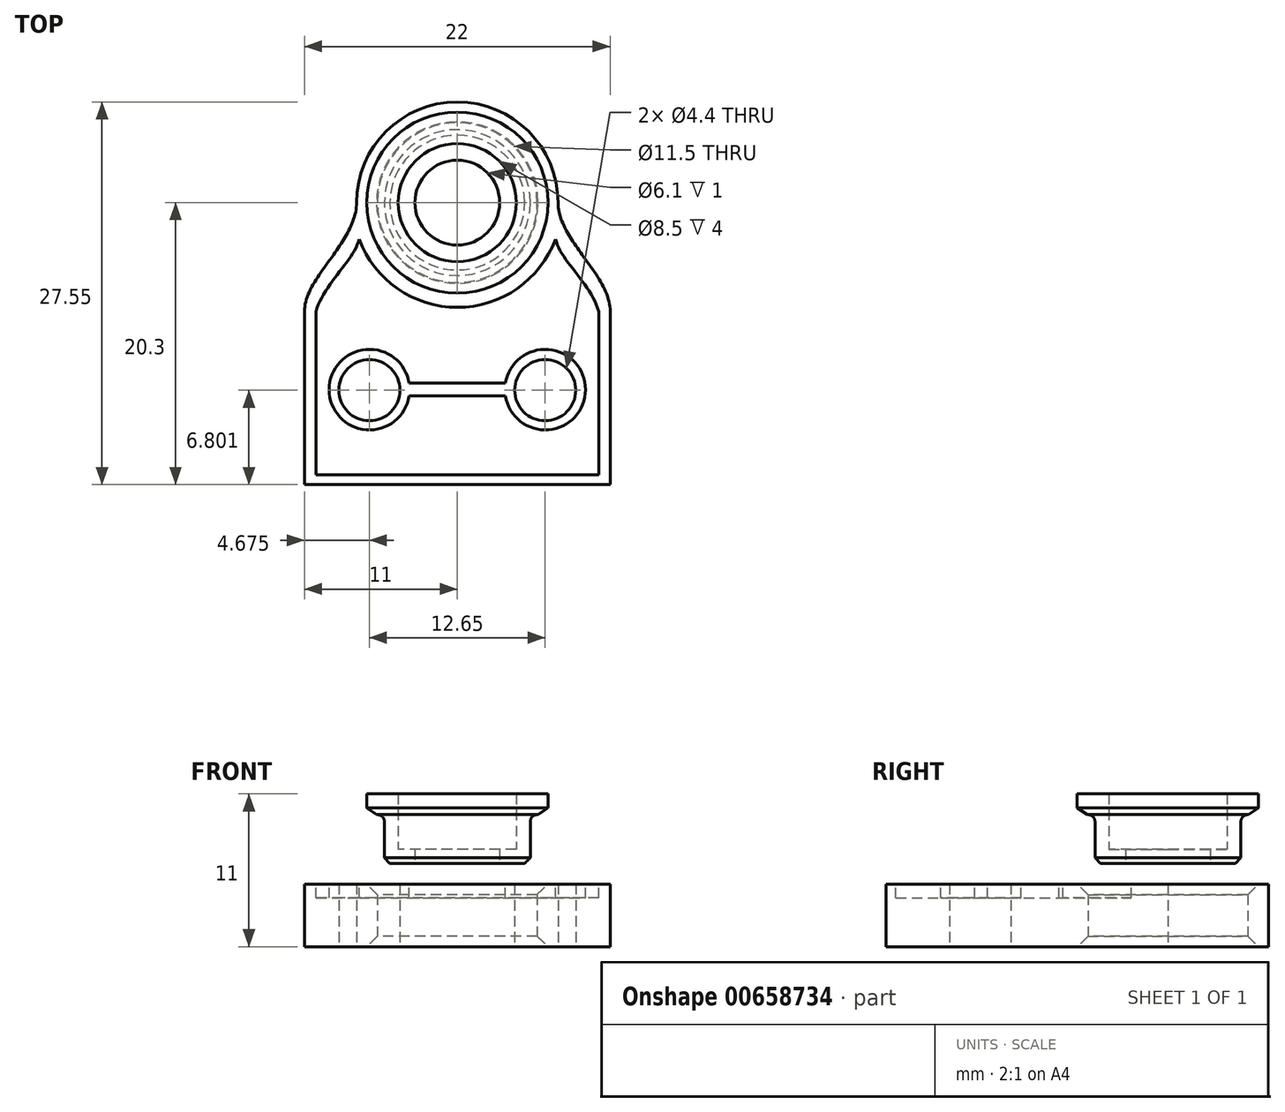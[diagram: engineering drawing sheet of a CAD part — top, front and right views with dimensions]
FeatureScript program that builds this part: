
annotation { "Feature Type Name" : "Feature", "Feature Type Description" : "" }
export const myFeature = defineFeature(function(context is Context, id is Id, definition is map)
    precondition{}
    {
        {
            var Q0;
            Q0=qCreatedBy(makeId("Top.planeOp"),FACE);
            var sketch = newSketch(context, id + "F0", { "sketchPlane" : qUnion([Q0])});
            skCircle(sketch, "E0", {"center": v(0, 0) * mm, "radius": 3.05 * mm});
            skCircle(sketch, "E1.0", {"center": v(0, 0) * mm, "radius": 4.25 * mm});
            skCircle(sketch, "E2.0", {"center": v(0, 0) * mm, "radius": 5.25 * mm});
            skSolve(sketch);
        }
        {
            var Q0;
            Q0=makeQuery(id+"F0.imprint","IMPRINT",FACE,{"disambiguationData":[TD([[makeQuery(id+"F0.imprint","IMPRINT",EDGE,{"derivedFrom":sQuery(id+"F0.wireOp",EDGE,"E0")}),-1.0]])]});
            extrude(context, id + "F1", {"entities" : qUnion([Q0]), "depth" : 1 * mm, "offsetDistance" : 25 * mm});
        }
        {
            var Q0;
            Q0=makeQuery(id+"F0.imprint","IMPRINT",FACE,{"disambiguationData":[TD([[makeQuery(id+"F0.imprint","IMPRINT",EDGE,{"derivedFrom":sQuery(id+"F0.wireOp",EDGE,"E1.0")}),-1.0]])]});
            extrude(context, id + "F2", {"entities" : qUnion([Q0]), "operationType" : NewBodyOperationType.ADD, "depth" : 5 * mm, "offsetDistance" : 25 * mm});
        }
        {
            var Q0;
            Q0=makeQuery(id+"F2.opExtrude","CAP_EDGE",EDGE,{"disambiguationData":[OSD([sQuery(id+"F0.wireOp",EDGE,"E2.0")])],"isStart":true});
            chamfer(context, id + "F3", {"entities" : qUnion([Q0]), "width" : .4 * mm, "tangentPropagation" : true});
        }
        {
            var Q0;
            Q0=qCreatedBy(makeId("Top.planeOp"),FACE);
            cPlane(context, id + "F4", {"entities" : qUnion([Q0]), "cplaneType" : CPlaneType.OFFSET, "offset" : 5 * mm, "width" : 150 * mm, "height" : 150 * mm});
        }
        {
            var Q0;
            Q0=qCreatedBy(id+"F4.planeOp",FACE);
            var sketch = newSketch(context, id + "F5", { "sketchPlane" : qUnion([Q0])});
            skCircle(sketch, "E3", {"center": v(0, 0) * mm, "radius": 4.84 * mm});
            skCircle(sketch, "E4", {"center": v(0, 0) * mm, "radius": 6.52 * mm});
            skSolve(sketch);
        }
        {
            var Q0;
            Q0 = qSketchRegion(id + "F5", true);
            extrude(context, id + "F6", {"entities" : qUnion([Q0]), "operationType" : NewBodyOperationType.ADD, "oppositeDirection" : true, "depth" : 1.5 * mm, "offsetDistance" : 25 * mm});
        }
        {
            var Q0;
            Q0=makeQuery(id+"F6.boolean.opBoolean","INTERSECT",EDGE,{"derivedFrom":[makeQuery(id+"F2.opExtrude","SWEPT_FACE",FACE,{"disambiguationData":[OSD([sQuery(id+"F0.wireOp",EDGE,"E2.0")])]}),makeQuery(id+"F6.opExtrude","CAP_FACE",FACE,{"disambiguationData":[OSD([sQuery(id+"F5.wireOp",EDGE,"E3"),sQuery(id+"F5.wireOp",EDGE,"E4")])],"isStart":false})]});
            fillet(context, id + "F7", {"entities" : qUnion([Q0]), "radius" : .5 * mm, "tangentPropagation" : true, "allowEdgeOverflow" : false});
        }
        {
            var Q0;
            Q0=makeQuery(id+"F6.opExtrude","CAP_EDGE",EDGE,{"disambiguationData":[OSD([sQuery(id+"F5.wireOp",EDGE,"E4")])],"isStart":false});
            chamfer(context, id + "F8", {"entities" : qUnion([Q0]), "chamferType" : ChamferType.OFFSET_ANGLE, "width" : .5 * mm, "oppositeDirection" : false, "angle" : 55 * degree, "tangentPropagation" : true});
        }
        {
            var Q0;
            Q0=qCreatedBy(makeId("Top.planeOp"),FACE);
            cPlane(context, id + "F9", {"entities" : qUnion([Q0]), "cplaneType" : CPlaneType.OFFSET, "offset" : 6 * mm, "oppositeDirection" : true, "width" : 150 * mm, "height" : 150 * mm});
        }
        {
            var Q0;
            Q0=qCreatedBy(id+"F9.planeOp",FACE);
            var sketch = newSketch(context, id + "F10", { "sketchPlane" : qUnion([Q0])});
            skCircle(sketch, "E5", {"center": v(0, 0) * mm, "radius": 5.75 * mm});
            skCircle(sketch, "E6.0", {"center": v(0, 0) * mm, "radius": 7.25 * mm});
            skLineSegment(sketch, "E7", {"start": v(0, 0) * mm, "end": v(11, 0) * mm});
            skLineSegment(sketch, "E8", {"start": v(0, 0) * mm, "end": v(-11, 0) * mm});
            skLineSegment(sketch, "E9", {"start": v(-11, 0) * mm, "end": v(-11, -20.3) * mm});
            skLineSegment(sketch, "E10.bottom", {"start": v(-11, -20.3) * mm, "end": v(11, -20.3) * mm});
            skLineSegment(sketch, "E10.top", {"start": v(-11, 0) * mm, "end": v(11, 0) * mm});
            skLineSegment(sketch, "E10.left", {"start": v(-11, -20.3) * mm, "end": v(-11, 0) * mm});
            skLineSegment(sketch, "E10.right", {"start": v(11, -20.3) * mm, "end": v(11, 0) * mm});
            skLineSegment(sketch, "E11", {"start": v(0, -20.3) * mm, "end": v(0, -8) * mm});
            skLineSegment(sketch, "E12", {"start": v(0, -8) * mm, "end": v(0, -13.5) * mm});
            skLineSegment(sketch, "E13", {"start": v(0, -13.5) * mm, "end": v(6.33, -13.5) * mm});
            skLineSegment(sketch, "E14", {"start": v(0, -13.5) * mm, "end": v(-6.33, -13.5) * mm});
            skCircle(sketch, "E15", {"center": v(6.33, -13.5) * mm, "radius": 2.2 * mm});
            skCircle(sketch, "E16", {"center": v(-6.33, -13.5) * mm, "radius": 2.2 * mm});
            skLineSegment(sketch, "E17", {"start": v(-11, 0) * mm, "end": v(-11, -3.75) * mm});
            skLineSegment(sketch, "E18", {"start": v(-11, -3.75) * mm, "end": v(11, -3.75) * mm});
            skLineSegment(sketch, "E19", {"start": v(11, 0) * mm, "end": v(11, -3.75) * mm});
            skFitSpline(sketch, "E20", {"points": [v(-7.25, 0) * mm, v(-11, -7.84) * mm], "startDerivative": vector(-0.1, -8.69) * mm, "endDerivative": vector(0, -7.46) * mm});
            skLineSegment(sketch, "E21", {"start": v(-11, -7.84) * mm, "end": v(11, -7.84) * mm});
            skFitSpline(sketch, "E22", {"points": [v(7.25, 0) * mm, v(11, -7.84) * mm], "startDerivative": vector(0.07, -8.24) * mm, "endDerivative": vector(0, -7.97) * mm});
            skSolve(sketch);
        }
        {
            var Q0;
            Q0=makeQuery(id+"F10.imprint","IMPRINT",FACE,{"disambiguationData":[TD([[makeQuery(id+"F10.imprint","IMPRINT",EDGE,{"derivedFrom":sQuery(id+"F10.wireOp",EDGE,"E5")}),-1.0]])]});
            var Q1;
            {var subQ1=sQuery(id+"F10.wireOp",EDGE,"E6.0");var subQ3=sQuery(id+"F10.wireOp",EDGE,"E18");var subQ4=makeQuery(id+"F10.imprint","INTERSECT",VERTEX,{"disambiguationData":[OD(0.0)],"derivedFrom":[subQ1,subQ3]});Q1=makeQuery(id+"F10.imprint","IMPRINT",FACE,{"disambiguationData":[TD([[makeQuery(id+"F10.imprint","IMPRINT",EDGE,{"disambiguationData":[TD([[subQ4,1.0]])],"derivedFrom":subQ3}),1.0]])]});}
            var Q2;
            {var subQ8=sQuery(id+"F10.wireOp",EDGE,"E21");Q2=makeQuery(id+"F10.imprint","IMPRINT",FACE,{"disambiguationData":[TD([[makeQuery(id+"F10.imprint","IMPRINT",EDGE,{"derivedFrom":subQ8}),1.0]])]});}
            var Q3;
            {var subQ1=sQuery(id+"F10.wireOp",EDGE,"E6.0");var subQ3=sQuery(id+"F10.wireOp",EDGE,"E18");var subQ4=makeQuery(id+"F10.imprint","INTERSECT",VERTEX,{"disambiguationData":[OD(1.0)],"derivedFrom":[subQ1,subQ3]});Q3=makeQuery(id+"F10.imprint","IMPRINT",FACE,{"disambiguationData":[TD([[makeQuery(id+"F10.imprint","IMPRINT",EDGE,{"disambiguationData":[TD([[subQ4,-1.0]])],"derivedFrom":subQ3}),1.0]])]});}
            var Q4;
            Q4=makeQuery(id+"F10.imprint","IMPRINT",FACE,{"disambiguationData":[TD([[makeQuery(id+"F10.imprint","IMPRINT",EDGE,{"derivedFrom":sQuery(id+"F10.wireOp",EDGE,"E15")}),-1.0]])]});
            extrude(context, id + "F11", {"entities" : qUnion([Q0, Q1, Q2, Q3, Q4]), "depth" : 4.5 * mm, "offsetDistance" : 25 * mm});
        }
        {
            var Q0;
            Q0=makeQuery(id+"F11.opExtrude","CAP_EDGE",EDGE,{"disambiguationData":[OSD([sQuery(id+"F10.wireOp",EDGE,"E5")])],"isStart":false});
            var Q1;
            Q1=makeQuery(id+"F11.opExtrude","CAP_EDGE",EDGE,{"disambiguationData":[OSD([sQuery(id+"F10.wireOp",EDGE,"E5")])],"isStart":true});
            chamfer(context, id + "F12", {"entities" : qUnion([Q0, Q1]), "width" : .75 * mm, "tangentPropagation" : true});
        }
        {
            var Q0;
            Q0=qCreatedBy(id+"F9.planeOp",FACE);
            cPlane(context, id + "F13", {"entities" : qUnion([Q0]), "cplaneType" : CPlaneType.OFFSET, "offset" : 4.5 * mm, "width" : 150 * mm, "height" : 150 * mm});
        }
        {
            var Q0;
            Q0=qCreatedBy(id+"F13.planeOp",FACE);
            var sketch = newSketch(context, id + "F14", { "sketchPlane" : qUnion([Q0])});
            skLineSegment(sketch, "E23", {"start": v(0, 0) * mm, "end": v(0, -7.54) * mm});
            skCircle(sketch, "E24", {"center": v(0, 0) * mm, "radius": 7.54 * mm});
            skLineSegment(sketch, "E25", {"start": v(0, -19.58) * mm, "end": v(-10.18, -19.58) * mm});
            skPoint(sketch, "E26.end.orphan", {"position": v(-10.18, -7.54) * mm});
            skLineSegment(sketch, "E27", {"start": v(-10.18, -19.58) * mm, "end": v(-10.18, -7.85) * mm});
            skFitSpline(sketch, "E28", {"points": [v(-10.18, -7.85) * mm, v(-7.07, -2.62) * mm], "startDerivative": vector(1.57, 5.95) * mm, "endDerivative": vector(1.03, 4.68) * mm});
            skLineSegment(sketch, "E29", {"start": v(0, -19.58) * mm, "end": v(0, -7.54) * mm});
            skLineSegment(sketch, "E30.MirrorCS", {"start": v(0, -19.58) * mm, "end": v(10.18, -19.58) * mm});
            skLineSegment(sketch, "E31.MirrorCS", {"start": v(10.18, -19.58) * mm, "end": v(10.18, -7.85) * mm});
            skFitSpline(sketch, "E32.MirrorCS", {"points": [v(10.18, -7.85) * mm, v(7.07, -2.62) * mm], "startDerivative": vector(-1.57, 5.95) * mm, "endDerivative": vector(-1.03, 4.68) * mm});
            skLineSegment(sketch, "E33", {"start": v(0, -13.56) * mm, "end": v(-6.33, -13.56) * mm});
            skLineSegment(sketch, "E34", {"start": v(0, -13.56) * mm, "end": v(6.33, -13.56) * mm});
            skCircle(sketch, "E35", {"center": v(-6.32, -13.46) * mm, "radius": 2.9 * mm});
            skCircle(sketch, "E36", {"center": v(6.33, -13.46) * mm, "radius": 2.9 * mm});
            skLineSegment(sketch, "E37", {"start": v(-3.46, -13) * mm, "end": v(3.46, -13) * mm});
            skLineSegment(sketch, "E38", {"start": v(-3.46, -13) * mm, "end": v(-3.46, -13.92) * mm});
            skLineSegment(sketch, "E39", {"start": v(-3.46, -13.92) * mm, "end": v(3.46, -13.92) * mm});
            skSolve(sketch);
        }
        {
            var Q0;
            {var subQ0=sQuery(id+"F14.wireOp",EDGE,"E25");Q0=makeQuery(id+"F14.imprint","IMPRINT",FACE,{"disambiguationData":[TD([[makeQuery(id+"F14.imprint","IMPRINT",EDGE,{"derivedFrom":subQ0}),-1.0]])]});}
            var Q1;
            {var subQ0=sQuery(id+"F14.wireOp",EDGE,"E30.MirrorCS");Q1=makeQuery(id+"F14.imprint","IMPRINT",FACE,{"disambiguationData":[TD([[makeQuery(id+"F14.imprint","IMPRINT",EDGE,{"derivedFrom":subQ0}),1.0]])]});}
            extrude(context, id + "F15", {"entities" : qUnion([Q0, Q1]), "operationType" : NewBodyOperationType.REMOVE, "oppositeDirection" : true, "depth" : 1 * mm, "offsetDistance" : 25 * mm});
        }
    });
